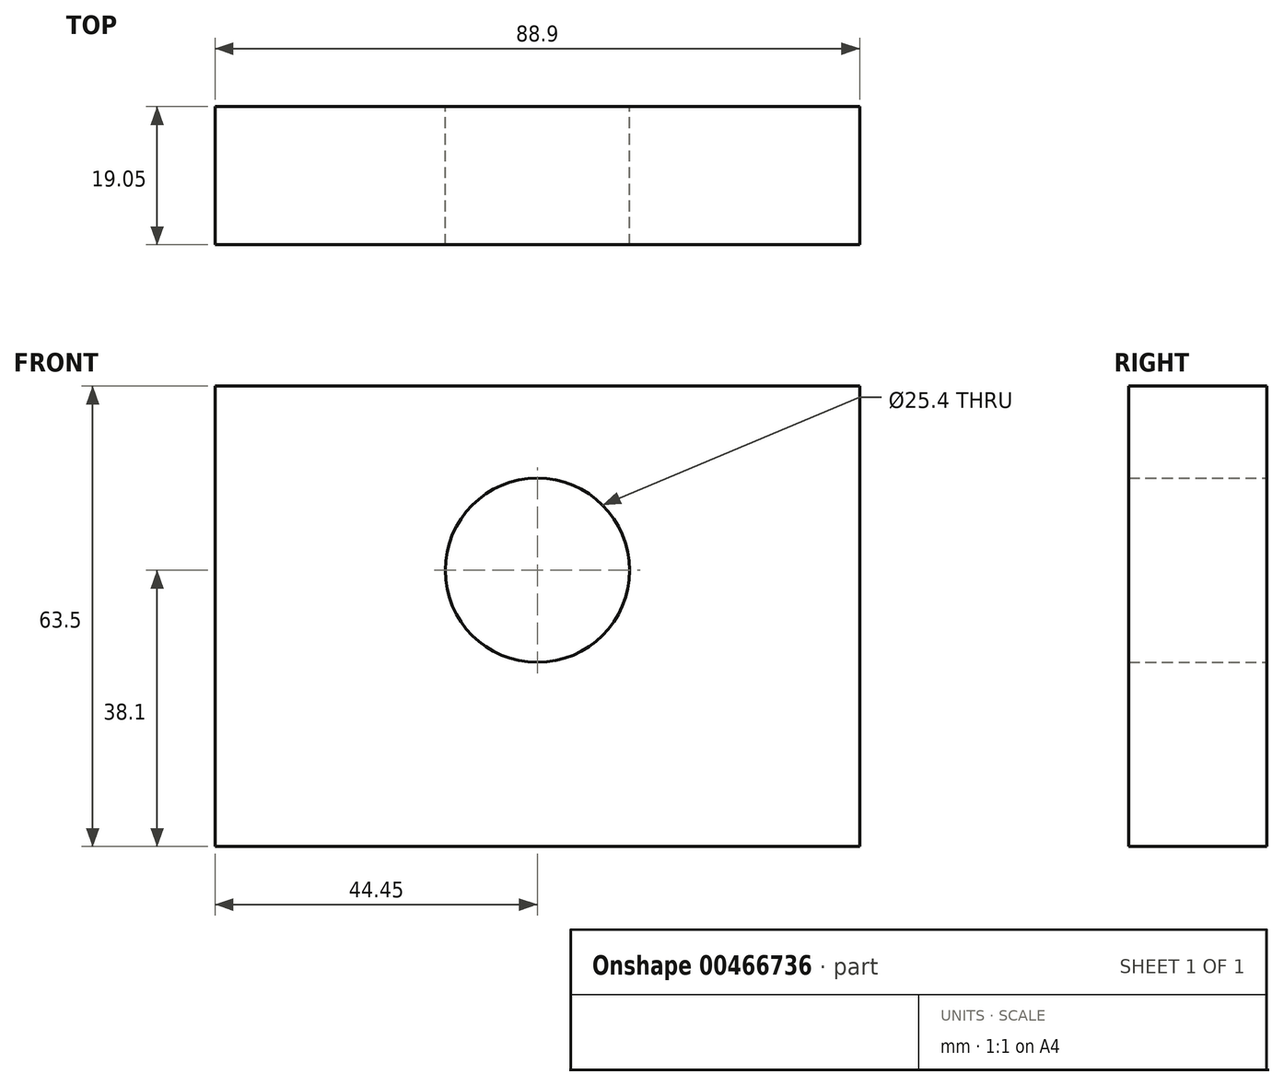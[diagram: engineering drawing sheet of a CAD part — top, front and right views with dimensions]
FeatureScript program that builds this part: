
annotation { "Feature Type Name" : "Feature", "Feature Type Description" : "" }
export const myFeature = defineFeature(function(context is Context, id is Id, definition is map)
    precondition{}
    {
        {
            var Q0;
            Q0=qCreatedBy(makeId("Front.planeOp"),FACE);
            var sketch = newSketch(context, id + "F0", { "sketchPlane" : qUnion([Q0])});
            skLineSegment(sketch, "E0.bottom", {"start": v(44.45, -31.75) * mm, "end": v(-44.45, -31.75) * mm});
            skLineSegment(sketch, "E0.top", {"start": v(44.45, 31.75) * mm, "end": v(-44.45, 31.75) * mm});
            skLineSegment(sketch, "E0.left", {"start": v(44.45, -31.75) * mm, "end": v(44.45, 31.75) * mm});
            skLineSegment(sketch, "E0.right", {"start": v(-44.45, -31.75) * mm, "end": v(-44.45, 31.75) * mm});
            skPoint(sketch, "E0.middle", {"position": v(0, 0) * mm});
            skCircle(sketch, "E1", {"center": v(0, 6.35) * mm, "radius": 12.7 * mm});
            skSolve(sketch);
        }
        {
            var Q0;
            Q0 = qSketchRegion(id + "F0", true);
            extrude(context, id + "F1", {"entities" : qUnion([Q0]), "depth" : 19.05 * mm});
        }
    });
